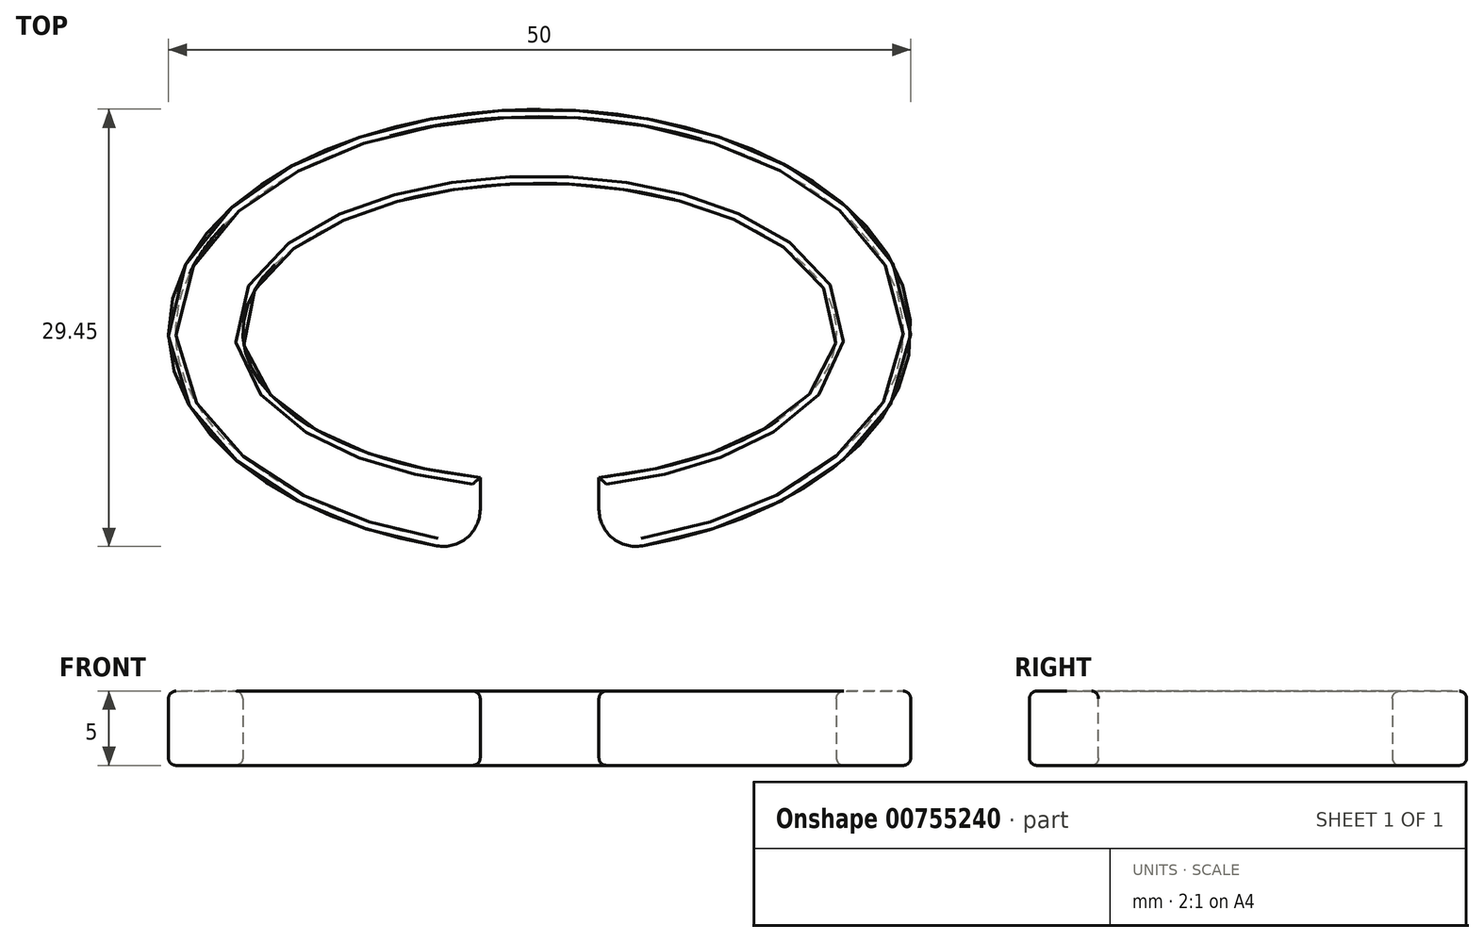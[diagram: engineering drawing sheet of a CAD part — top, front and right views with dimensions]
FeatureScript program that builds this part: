
annotation { "Feature Type Name" : "Feature", "Feature Type Description" : "" }
export const myFeature = defineFeature(function(context is Context, id is Id, definition is map)
    precondition{}
    {
        {
            var Q0;
            Q0=qCreatedBy(makeId("Top.planeOp"),FACE);
            var sketch = newSketch(context, id + "F0", { "sketchPlane" : qUnion([Q0])});
            skEllipse(sketch, "E0", {"center": v(0, 0) * mm, "majorRadius": 25 * mm, "minorRadius": 15 * mm, "majorAxis": v(1, 0)});
            skSolve(sketch);
        }
        {
            var Q0;
            Q0=makeQuery(id+"F0.imprint","IMPRINT",FACE,{"disambiguationData":[TD([[makeQuery(id+"F0.imprint","IMPRINT",EDGE,{"derivedFrom":sQuery(id+"F0.wireOp",EDGE,"E0")}),1.0]])]});
            extrude(context, id + "F1", {"entities" : qUnion([Q0]), "depth" : 5 * mm, "offsetDistance" : 25 * mm});
        }
        {
            var Q0;
            Q0=makeQuery(id+"F1.opExtrude","CAP_FACE",FACE,{"disambiguationData":[OSD([sQuery(id+"F0.wireOp",EDGE,"E0")])],"isStart":false});
            var sketch = newSketch(context, id + "F2", { "sketchPlane" : qUnion([Q0])});
            skEllipse(sketch, "E1", {"center": v(0, 0) * mm, "majorRadius": 20 * mm, "minorRadius": 10 * mm, "majorAxis": v(1, 0)});
            skSolve(sketch);
        }
        {
            var Q0;
            Q0=makeQuery(id+"F2.imprint","IMPRINT",FACE,{"disambiguationData":[TD([[makeQuery(id+"F2.imprint","IMPRINT",EDGE,{"derivedFrom":sQuery(id+"F2.wireOp",EDGE,"E1")}),1.0]])]});
            extrude(context, id + "F3", {"entities" : qUnion([Q0]), "operationType" : NewBodyOperationType.REMOVE, "oppositeDirection" : true, "depth" : 5 * mm, "offsetDistance" : 25 * mm});
        }
        {
            var Q0;
            Q0=makeQuery(id+"F1.opExtrude","CAP_FACE",FACE,{"disambiguationData":[OSD([sQuery(id+"F0.wireOp",EDGE,"E0")])],"isStart":false});
            var sketch = newSketch(context, id + "F4", { "sketchPlane" : qUnion([Q0])});
            skLineSegment(sketch, "E2.bottom", {"start": v(-4, -14.8) * mm, "end": v(4, -14.8) * mm});
            skLineSegment(sketch, "E2.top", {"start": v(-4, -5.2) * mm, "end": v(4, -5.2) * mm});
            skLineSegment(sketch, "E2.left", {"start": v(-4, -14.8) * mm, "end": v(-4, -5.2) * mm});
            skLineSegment(sketch, "E2.right", {"start": v(4, -14.8) * mm, "end": v(4, -5.2) * mm});
            skPoint(sketch, "E2.middle", {"position": v(0, -10) * mm});
            skSolve(sketch);
        }
        {
            var Q0;
            {var subQ0=sQuery(id+"F4.wireOp",EDGE,"E2.bottom");Q0=makeQuery(id+"F4.imprint","IMPRINT",FACE,{"disambiguationData":[TD([[makeQuery(id+"F4.imprint","IMPRINT",EDGE,{"derivedFrom":subQ0}),1.0]])]});}
            extrude(context, id + "F5", {"entities" : qUnion([Q0]), "operationType" : NewBodyOperationType.REMOVE, "oppositeDirection" : true, "depth" : 5 * mm, "offsetDistance" : 25 * mm});
        }
        {
            var Q0;
            {var subQ0=sQuery(id+"F0.wireOp",EDGE,"E0");Q0=makeQuery(id+"F5.boolean.opBoolean","SPLIT",FACE,{"disambiguationData":[TD([makeQuery(id+"F5.opExtrude","SWEPT_FACE",FACE,{"disambiguationData":[OSD([sQuery(id+"F4.wireOp",EDGE,"E2.bottom")])]})])],"derivedFrom":makeQuery(id+"F1.opExtrude","CAP_FACE",FACE,{"disambiguationData":[OSD([subQ0])],"isStart":false})});}
            extrude(context, id + "F6", {"entities" : qUnion([Q0]), "operationType" : NewBodyOperationType.REMOVE, "oppositeDirection" : true, "depth" : 5 * mm, "offsetDistance" : 25 * mm});
        }
        {
            var Q0;
            {var subQ0=sQuery(id+"F0.wireOp",EDGE,"E0");var subQ1=sQuery(id+"F4.wireOp",EDGE,"E2.left");Q0=makeQuery(id+"F5.boolean.opBoolean","COPY",EDGE,{"disambiguationData":[topologyDisambiguationEdgeConnected([makeQuery(id+"F5.opExtrude","SWEPT_FACE",FACE,{"disambiguationData":[OSD([subQ1])]})])],"derivedFrom":makeQuery(id+"F5.opExtrude","SWEPT_EDGE",EDGE,{"disambiguationData":[OSD([subQ0,sQuery(id+"F4.wireOp",EDGE,"E2.bottom"),subQ1])]})});}
            var Q1;
            Q1=makeQuery(id+"F5.boolean.opBoolean","COPY",EDGE,{"derivedFrom":makeQuery(id+"F5.opExtrude","SWEPT_EDGE",EDGE,{"disambiguationData":[OSD([sQuery(id+"F2.wireOp",EDGE,"E1"),sQuery(id+"F4.wireOp",EDGE,"E2.left")])]})});
            var Q2;
            Q2=makeQuery(id+"F5.boolean.opBoolean","COPY",EDGE,{"derivedFrom":makeQuery(id+"F5.opExtrude","SWEPT_EDGE",EDGE,{"disambiguationData":[OSD([sQuery(id+"F2.wireOp",EDGE,"E1"),sQuery(id+"F4.wireOp",EDGE,"E2.right")])]})});
            var Q3;
            {var subQ0=sQuery(id+"F0.wireOp",EDGE,"E0");var subQ1=sQuery(id+"F4.wireOp",EDGE,"E2.right");Q3=makeQuery(id+"F5.boolean.opBoolean","COPY",EDGE,{"disambiguationData":[topologyDisambiguationEdgeConnected([makeQuery(id+"F5.opExtrude","SWEPT_FACE",FACE,{"disambiguationData":[OSD([subQ1])]})])],"derivedFrom":makeQuery(id+"F5.opExtrude","SWEPT_EDGE",EDGE,{"disambiguationData":[OSD([subQ0,sQuery(id+"F4.wireOp",EDGE,"E2.bottom"),subQ1])]})});}
            fillet(context, id + "F7", {"entities" : qUnion([Q0, Q1, Q2, Q3]), "radius" : 2.5 * mm, "tangentPropagation" : true, "allowEdgeOverflow" : false});
        }
        {
            var Q0;
            {var subQ0=sQuery(id+"F0.wireOp",EDGE,"E0");Q0=makeQuery(id+"F5.boolean.opBoolean","SPLIT",FACE,{"disambiguationData":[TD([makeQuery(id+"F3.boolean.opBoolean","COPY",FACE,{"derivedFrom":makeQuery(id+"F3.opExtrude","SWEPT_FACE",FACE,{"disambiguationData":[OSD([sQuery(id+"F2.wireOp",EDGE,"E1")])]})})])],"derivedFrom":makeQuery(id+"F1.opExtrude","CAP_FACE",FACE,{"disambiguationData":[OSD([subQ0])],"isStart":false})});}
            var Q1;
            {var subQ0=sQuery(id+"F0.wireOp",EDGE,"E0");Q1=makeQuery(id+"F5.boolean.opBoolean","SPLIT",FACE,{"disambiguationData":[TD([makeQuery(id+"F3.boolean.opBoolean","COPY",FACE,{"derivedFrom":makeQuery(id+"F3.opExtrude","SWEPT_FACE",FACE,{"disambiguationData":[OSD([sQuery(id+"F2.wireOp",EDGE,"E1")])]})})])],"derivedFrom":makeQuery(id+"F1.opExtrude","CAP_FACE",FACE,{"disambiguationData":[OSD([subQ0])],"isStart":true})});}
            fillet(context, id + "F8", {"entities" : qUnion([Q0, Q1]), "radius" : .5 * mm, "tangentPropagation" : true, "allowEdgeOverflow" : false});
        }
    });
